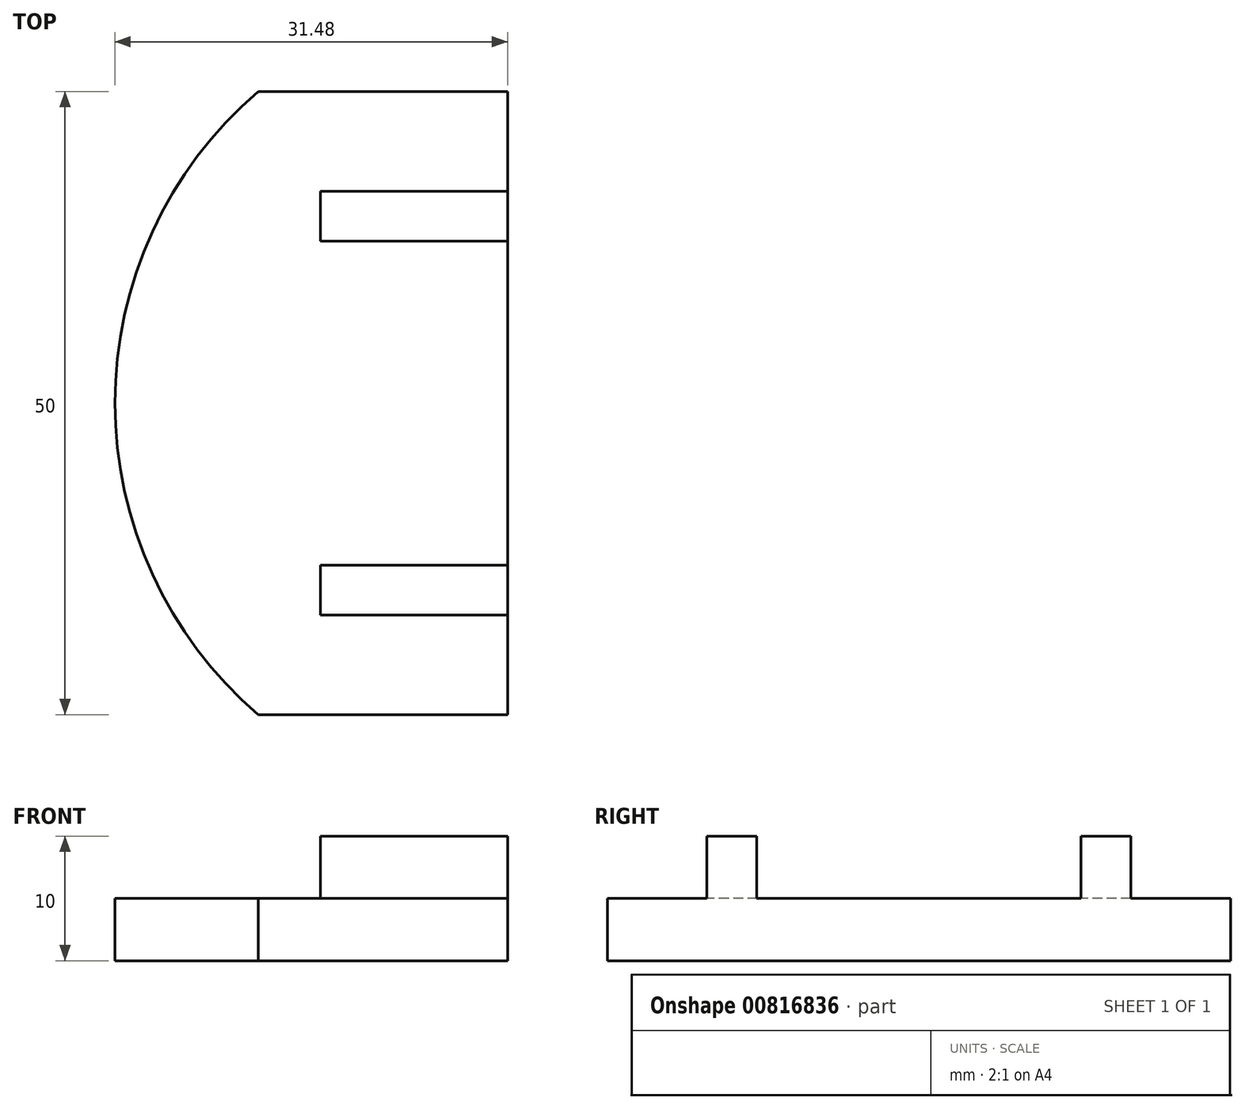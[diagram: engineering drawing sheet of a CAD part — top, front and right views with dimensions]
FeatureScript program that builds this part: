
annotation { "Feature Type Name" : "Feature", "Feature Type Description" : "" }
export const myFeature = defineFeature(function(context is Context, id is Id, definition is map)
    precondition{}
    {
        {
            var Q0;
            Q0=qCreatedBy(makeId("Top.planeOp"),FACE);
            var sketch = newSketch(context, id + "F0", { "sketchPlane" : qUnion([Q0])});
            skLineSegment(sketch, "E0.bottom", {"start": v(-10, -25) * mm, "end": v(10, -25) * mm});
            skLineSegment(sketch, "E0.top", {"start": v(-10, 25) * mm, "end": v(10, 25) * mm});
            skLineSegment(sketch, "E0.left", {"start": v(-10, -25) * mm, "end": v(-10, 25) * mm});
            skLineSegment(sketch, "E0.right", {"start": v(10, -25) * mm, "end": v(10, 25) * mm});
            skPoint(sketch, "E0.middle", {"position": v(0, 0) * mm});
            skArc(sketch, "E1", {"start": v(-10, 25) * mm, "mid": v(-21.48, 0) * mm, "end": v(-10, -25) * mm});
            skSolve(sketch);
        }
        {
            var Q0;
            Q0=qSketchRegion(id+"F0",true);
            extrude(context, id + "F1", {"entities" : qUnion([Q0]), "depth" : 5 * mm, "offsetDistance" : 25 * mm});
        }
        {
            var Q0;
            Q0=makeQuery(id+"F1.opExtrude","CAP_FACE",FACE,{"disambiguationData":[OSD([sQuery(id+"F0.wireOp",EDGE,"E0.bottom"),sQuery(id+"F0.wireOp",EDGE,"E0.top"),sQuery(id+"F0.wireOp",EDGE,"E0.right"),sQuery(id+"F0.wireOp",EDGE,"E1")])],"isStart":false});
            var sketch = newSketch(context, id + "F2", { "sketchPlane" : qUnion([Q0])});
            skLineSegment(sketch, "E2.bottom", {"start": v(10, 17) * mm, "end": v(-5, 17) * mm});
            skLineSegment(sketch, "E2.top", {"start": v(10, 13) * mm, "end": v(-5, 13) * mm});
            skLineSegment(sketch, "E2.left", {"start": v(10, 17) * mm, "end": v(10, 13) * mm});
            skLineSegment(sketch, "E2.right", {"start": v(-5, 17) * mm, "end": v(-5, 13) * mm});
            skLineSegment(sketch, "E3.bottom", {"start": v(10, -13) * mm, "end": v(-5, -13) * mm});
            skLineSegment(sketch, "E3.top", {"start": v(10, -17) * mm, "end": v(-5, -17) * mm});
            skLineSegment(sketch, "E3.left", {"start": v(10, -13) * mm, "end": v(10, -17) * mm});
            skLineSegment(sketch, "E3.right", {"start": v(-5, -13) * mm, "end": v(-5, -17) * mm});
            skSolve(sketch);
        }
        {
            var Q0;
            Q0=qSketchRegion(id+"F2",true);
            extrude(context, id + "F3", {"entities" : qUnion([Q0]), "operationType" : NewBodyOperationType.ADD, "depth" : 5 * mm, "offsetDistance" : 25 * mm});
        }
    });
